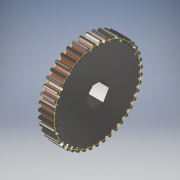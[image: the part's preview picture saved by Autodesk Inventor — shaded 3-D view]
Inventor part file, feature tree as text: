
AUTODESK INVENTOR PART (.ipt)
format: ipt  version: 2018 (Build 220112000, 112)  size: 323,072 bytes
history: native  units: in
note: dims shown in document units (in); Inventor stores cm internally (conversion verified against a paired STEP export)
features: other x3, sketch x1
ambient origin geometry x8: Origin, YZ Plane, XZ Plane, XY Plane, X Axis, Y Axis, Z Axis, Center Point
bodies: Solid1 (feature_tree)
feature tree (4):
  sketch  "Sketch1"  dims[d0=2.15in d1=1.0in d2=0.0in]
  other  "Srf1"
  other  "Cut-Extrude1"
  other  "pitch circle"
